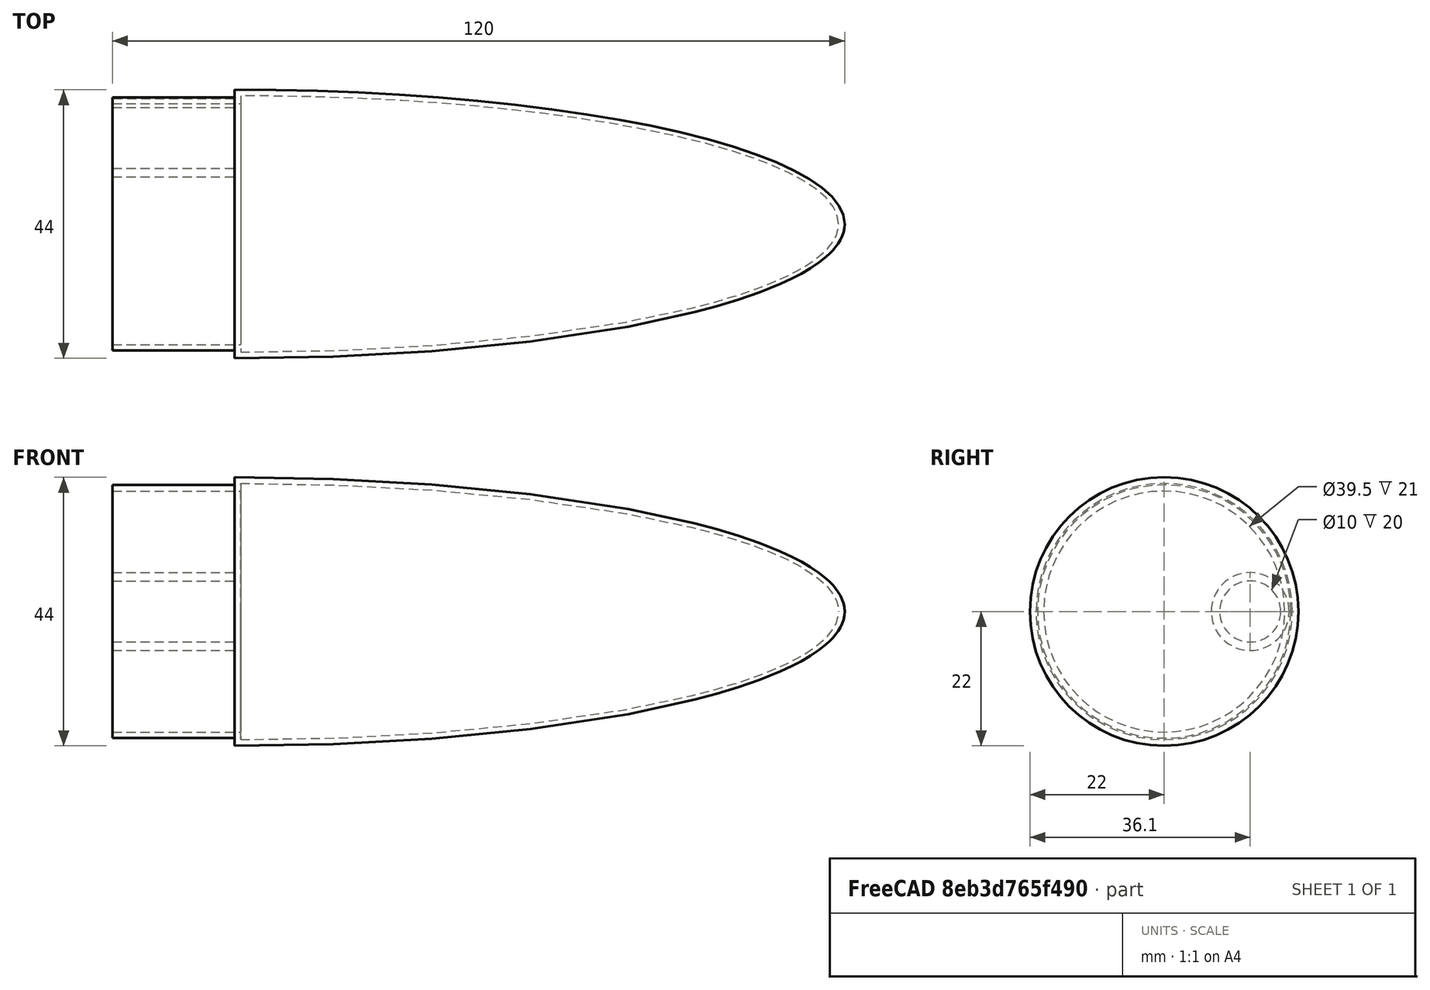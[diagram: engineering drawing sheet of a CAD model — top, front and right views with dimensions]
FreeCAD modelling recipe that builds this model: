
FCSTD DOCUMENT  (FreeCAD 0.20R29603 (Git))
Label: TP Nose Cone Retry
License: All rights reserved
LicenseURL: http://en.wikipedia.org/wiki/All_rights_reserved
objects: Part::FeaturePython×1, Sketcher::SketchObject×1, PartDesign::Pad×1, PartDesign::Hole×1, PartDesign::Body×1
note: 7 computed .brp shape members not serialized (recipe doc carries the construction recipe); baked Part::Feature solids carry a one-line shape summary decoded from their .brp

FEATURE [Part::FeaturePython] NoseCone  # WARN: FeaturePython — macro-defined, semantics opaque (R4)
  Coefficient = 0
  Diameter = 44
  Length = 100
  NoseStyle = 1
  NoseType = 1
  Resolution = 100
  Shoulder = true
  ShoulderDiameter = 41.5
  ShoulderLength = 20
  ShoulderThickness = 1
  Thickness = 1
FEATURE [Sketcher::SketchObject] Sketch
  FullyConstrained = false
  MapMode = 5
  Placement = pos=(0,0,0) rot=(0.57735,0.57735,0.57735;2.0944rad)
  Support = -> [YZ_Plane]
  sketch-geometry (1):
    g0: Circle CenterX=14.1 CenterY=0 CenterZ=0 NormalX=0 NormalY=0 NormalZ=1 AngleXU=0 Radius=6.37425
  constraints (2):
    c: PointOnObject(g0,g-1)
    c: DistanceX(g-1,g0) = 14.1
FEATURE [PartDesign::Pad] Pad
  Direction = (1,-2e-16,3e-16)
  Length = 20
  Length2 = 10
  Placement = pos=(0,0,0) rot=(0.57735,0.57735,0.57735;2.0944rad)
  Profile = -> Sketch
  ReferenceAxis = -> Sketch [N_Axis]
  Reversed = true
  Type = 0
FEATURE [PartDesign::Hole] Hole
  BaseFeature = -> Pad
  CustomThreadClearance = 0
  Depth = 25
  DepthType = 0
  Diameter = 10
  DrillForDepth = false
  DrillPoint = 1
  DrillPointAngle = 118
  HoleCutCountersinkAngle = 90
  HoleCutCustomValues = false
  HoleCutDepth = 0
  HoleCutDiameter = 6.1
  HoleCutType = 0
  ModelThread = false
  Placement = pos=(0,0,0) rot=(0.57735,0.57735,0.57735;2.0944rad)
  Profile = -> Pad [Face3]
  Tapered = false
  TaperedAngle = 90
  ThreadClass = 0
  ThreadDepth = 25
  ThreadDepthType = 0
  ThreadDirection = 0
  ThreadFit = 0
  ThreadSize = 0
  ThreadType = 0
  Threaded = false
  UseCustomThreadClearance = false
FEATURE [PartDesign::Body] Body
  Group = -> [Sketch,Pad,Hole]
  Origin = -> Origin
  Tip = -> Hole
